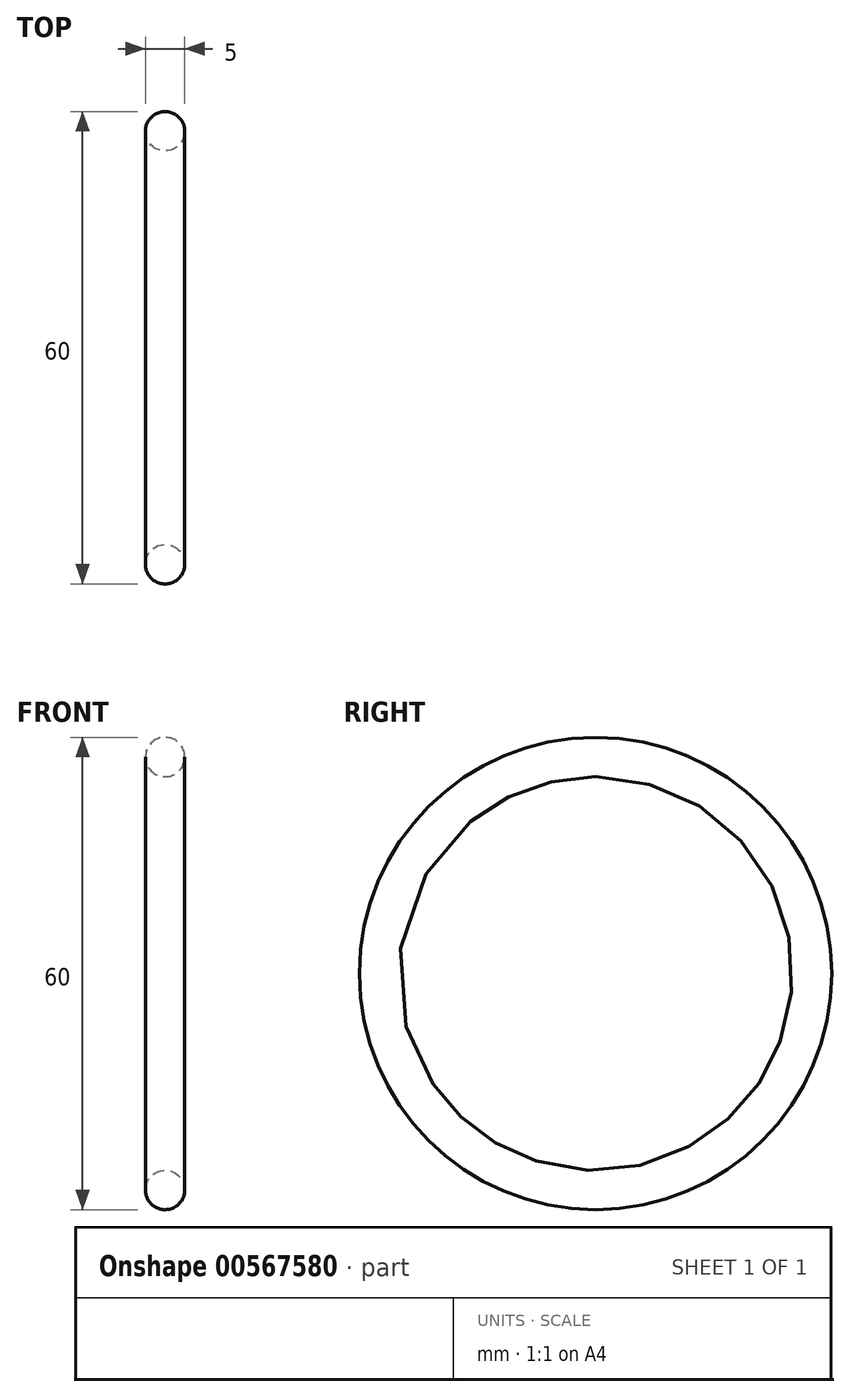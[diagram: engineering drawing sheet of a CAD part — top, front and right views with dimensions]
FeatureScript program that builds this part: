
annotation { "Feature Type Name" : "Feature", "Feature Type Description" : "" }
export const myFeature = defineFeature(function(context is Context, id is Id, definition is map)
    precondition{}
    {
        {
            var Q0;
            Q0=qCreatedBy(makeId("Front.planeOp"),FACE);
            var sketch = newSketch(context, id + "F0", { "sketchPlane" : qUnion([Q0])});
            skCircle(sketch, "E0", {"center": v(0, 27.5) * mm, "radius": 2.5 * mm});
            skLineSegment(sketch, "E1", {"start": v(-3.61, 0) * mm, "end": v(5.16, 0) * mm, "construction": true});
            skSolve(sketch);
        }
        {
            var Q0;
            Q0 = qSketchRegion(id + "F0", true);
            var Q1;
            Q1=sQuery(id+"F0.wireOp",EDGE,"E1");
            revolve(context, id + "F1", {"entities" : qUnion([Q0]), "axis" : qUnion([Q1]), "revolveType" : RevolveType.FULL});
        }
    });
